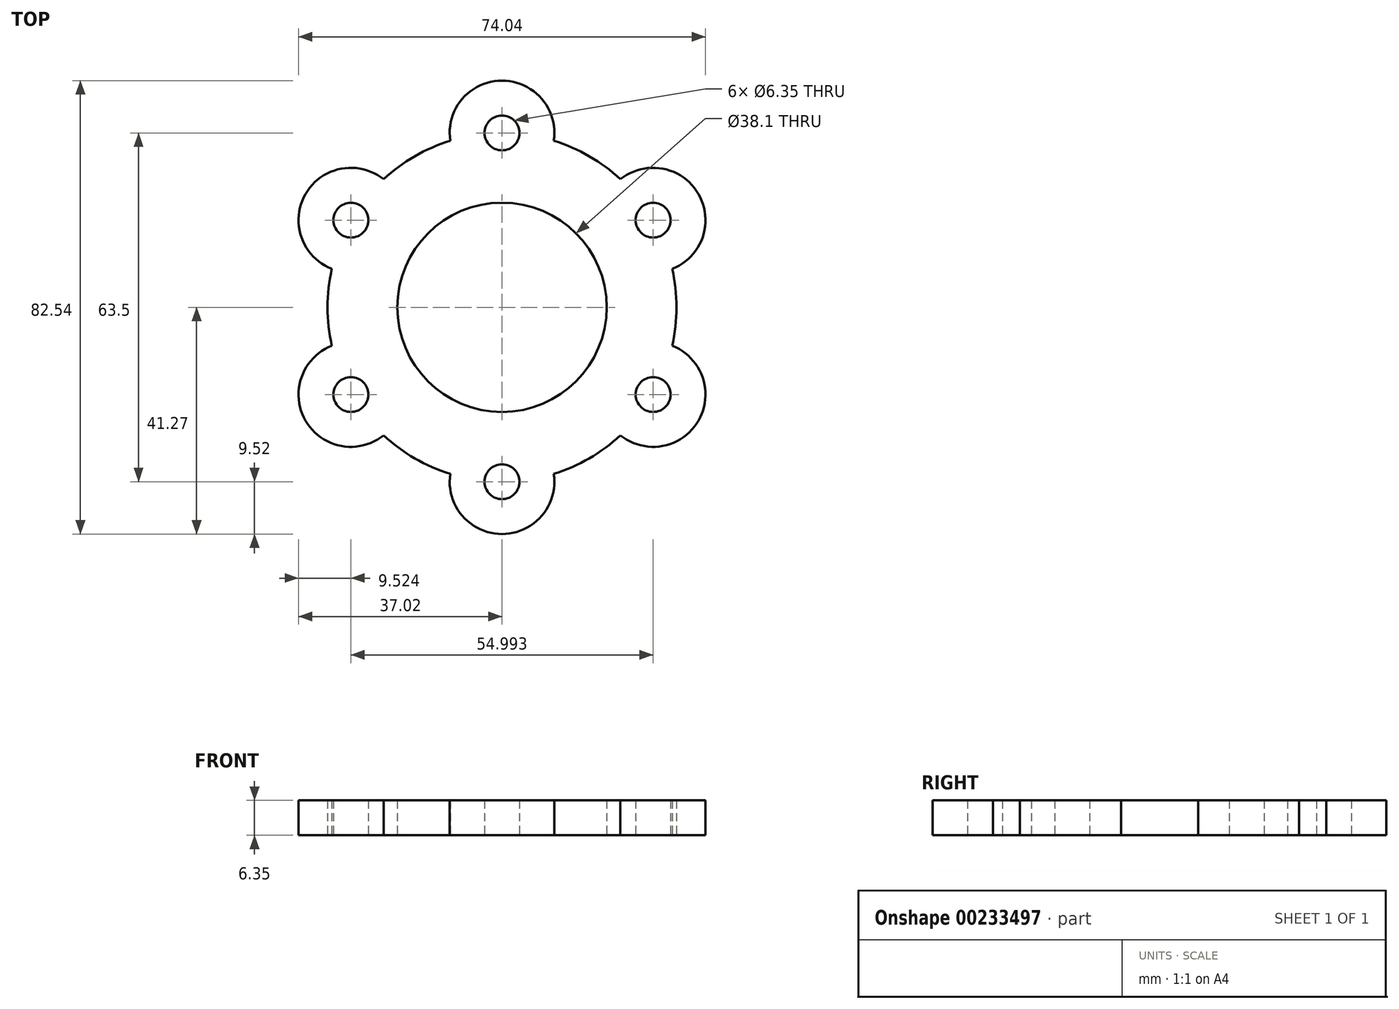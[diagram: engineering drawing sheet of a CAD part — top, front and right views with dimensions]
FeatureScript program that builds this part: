
annotation { "Feature Type Name" : "Feature", "Feature Type Description" : "" }
export const myFeature = defineFeature(function(context is Context, id is Id, definition is map)
    precondition{}
    {
        {
            var Q0;
            Q0=qCreatedBy(makeId("Top.planeOp"),FACE);
            var sketch = newSketch(context, id + "F0", { "sketchPlane" : qUnion([Q0])});
            skCircle(sketch, "E0", {"center": v(0, 0) * mm, "radius": 19.05 * mm});
            skCircle(sketch, "E1", {"center": v(0, 0) * mm, "radius": 31.75 * mm});
            skCircle(sketch, "E2.cCircle", {"center": v(0, 0) * mm, "radius": 31.75 * mm, "construction": true});
            skCircle(sketch, "E3", {"center": v(0, 31.75) * mm, "radius": 3.18 * mm});
            skCircle(sketch, "E4", {"center": v(0, 31.75) * mm, "radius": 9.53 * mm});
            skCircle(sketch, "E5.1.0", {"center": v(-27.5, 15.88) * mm, "radius": 3.18 * mm});
            skCircle(sketch, "E5.1.1", {"center": v(-27.5, 15.88) * mm, "radius": 9.53 * mm});
            skCircle(sketch, "E5.2.0", {"center": v(-27.5, -15.87) * mm, "radius": 3.18 * mm});
            skCircle(sketch, "E5.2.1", {"center": v(-27.5, -15.87) * mm, "radius": 9.53 * mm});
            skCircle(sketch, "E5.3.0", {"center": v(0, -31.75) * mm, "radius": 3.18 * mm});
            skCircle(sketch, "E5.3.1", {"center": v(0, -31.75) * mm, "radius": 9.53 * mm});
            skCircle(sketch, "E5.4.0", {"center": v(27.5, -15.88) * mm, "radius": 3.18 * mm});
            skCircle(sketch, "E5.4.1", {"center": v(27.5, -15.88) * mm, "radius": 9.53 * mm});
            skCircle(sketch, "E5.5.0", {"center": v(27.5, 15.88) * mm, "radius": 3.18 * mm});
            skCircle(sketch, "E5.5.1", {"center": v(27.5, 15.88) * mm, "radius": 9.53 * mm});
            skSolve(sketch);
        }
        {
            var Q0;
            Q0 = qSketchRegion(id + "F0", true);
            extrude(context, id + "F1", {"entities" : qUnion([Q0]), "depth" : 6.35 * mm});
        }
    });
